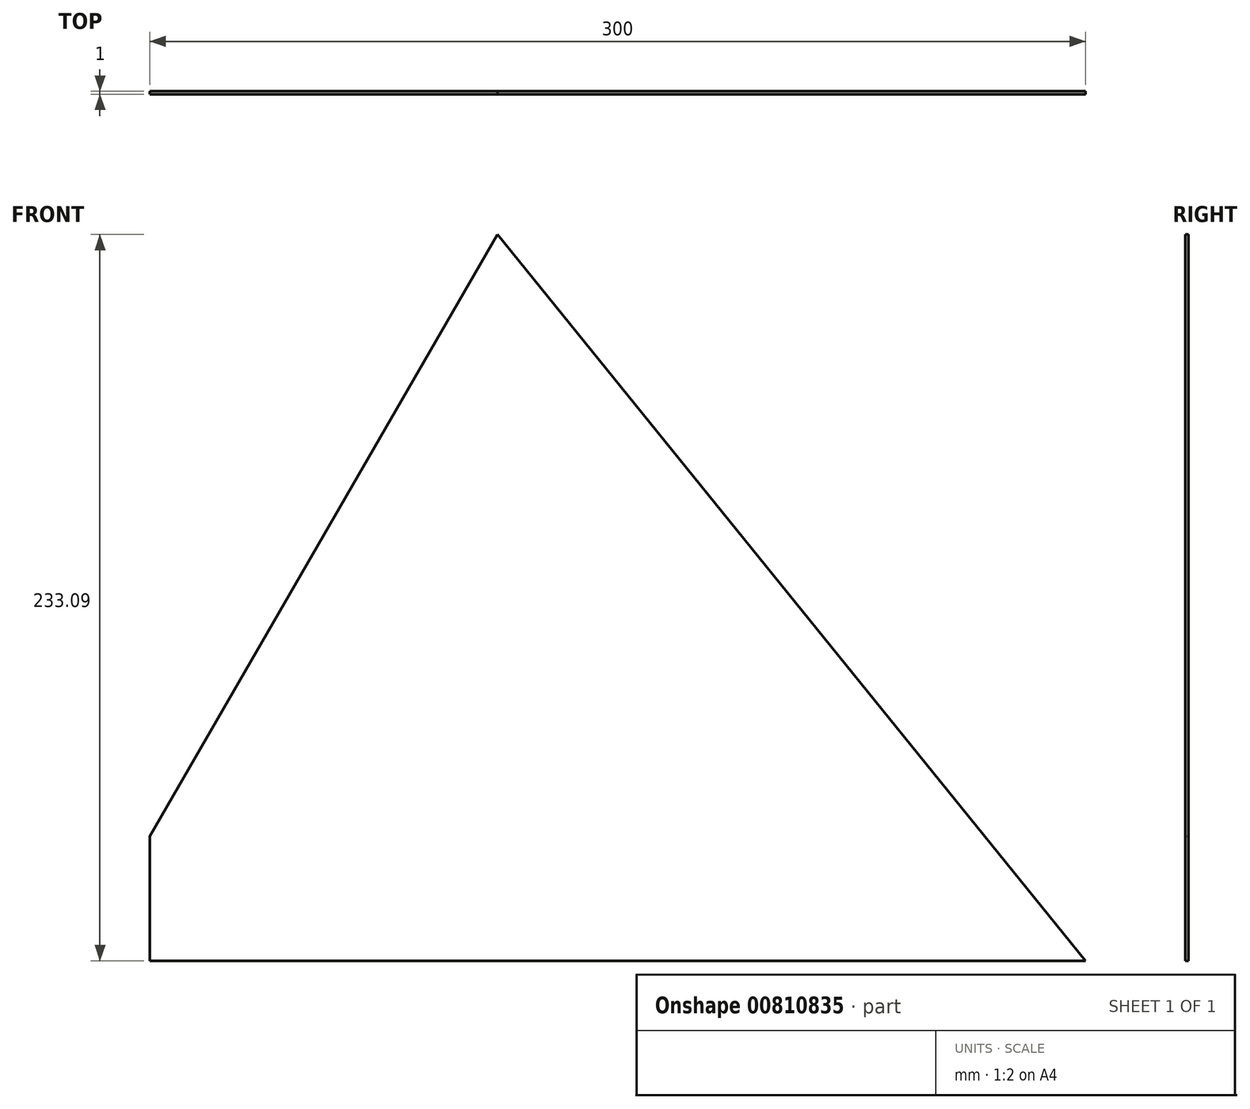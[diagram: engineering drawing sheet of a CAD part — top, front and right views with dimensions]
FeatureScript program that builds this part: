
annotation { "Feature Type Name" : "Feature", "Feature Type Description" : "" }
export const myFeature = defineFeature(function(context is Context, id is Id, definition is map)
    precondition{}
    {
        {
            var Q0;
            Q0=qCreatedBy(makeId("Front.planeOp"),FACE);
            var sketch = newSketch(context, id + "F0", { "sketchPlane" : qUnion([Q0])});
            skLineSegment(sketch, "E0", {"start": v(-300, 0) * mm, "end": v(0, 0) * mm});
            skLineSegment(sketch, "E1", {"start": v(0, 0) * mm, "end": v(0, 559.62) * mm});
            skLineSegment(sketch, "E2", {"start": v(0, 559.62) * mm, "end": v(-323.1, 0) * mm});
            skLineSegment(sketch, "E3", {"start": v(-323.1, 0) * mm, "end": v(-300, 0) * mm});
            skLineSegment(sketch, "E4", {"start": v(-300, 0) * mm, "end": v(-300, 40) * mm});
            skLineSegment(sketch, "E5", {"start": v(0, 0) * mm, "end": v(-188.52, 233.09) * mm});
            skSolve(sketch);
        }
        {
            var Q0;
            Q0=makeQuery(id+"F0.imprint","IMPRINT",FACE,{"disambiguationData":[TD([[makeQuery(id+"F0.imprint","IMPRINT",EDGE,{"derivedFrom":sQuery(id+"F0.wireOp",EDGE,"E0")}),1.0]])]});
            extrude(context, id + "F1", {"entities" : qUnion([Q0]), "depth" : 1 * mm, "offsetDistance" : 25 * mm});
        }
    });
